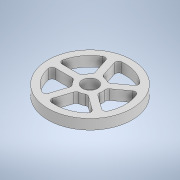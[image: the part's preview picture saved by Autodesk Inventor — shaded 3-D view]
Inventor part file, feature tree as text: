
AUTODESK INVENTOR PART (.ipt)
format: ipt  version: 2020 (Build 240168000, 168)  size: 187,392 bytes
history: native  units: mm
features: extrude x1, fillet x1, pattern_circular x1, sketch x1
ambient origin geometry x8: Origin, YZ Plane, XZ Plane, XY Plane, X Axis, Y Axis, Z Axis, Center Point
bodies: Solid1 (feature_tree)
feature tree (4):
  extrude  "Extrusion1"  Depth=2.0mm
  fillet  "Fillet1"  Radius=3.0mm
  pattern_circular  "Circular Pattern1"  [2 undecoded]
  sketch  "Sketch1"  dims[d0=9.0mm d1=50.0mm d2=3.0mm d3=4.0mm d4=4.0mm d5=20.0mm d6=50.0mm d8=360.0deg d10=6.0mm d11=0.0mm d12=2.0mm d13=50.0mm d14=360.0deg]
note: 2 required parameter values undecoded (feature->parameter linkage not recoverable at this tier; creation-order binding heuristic only, values carry confidence <= 0.55)
